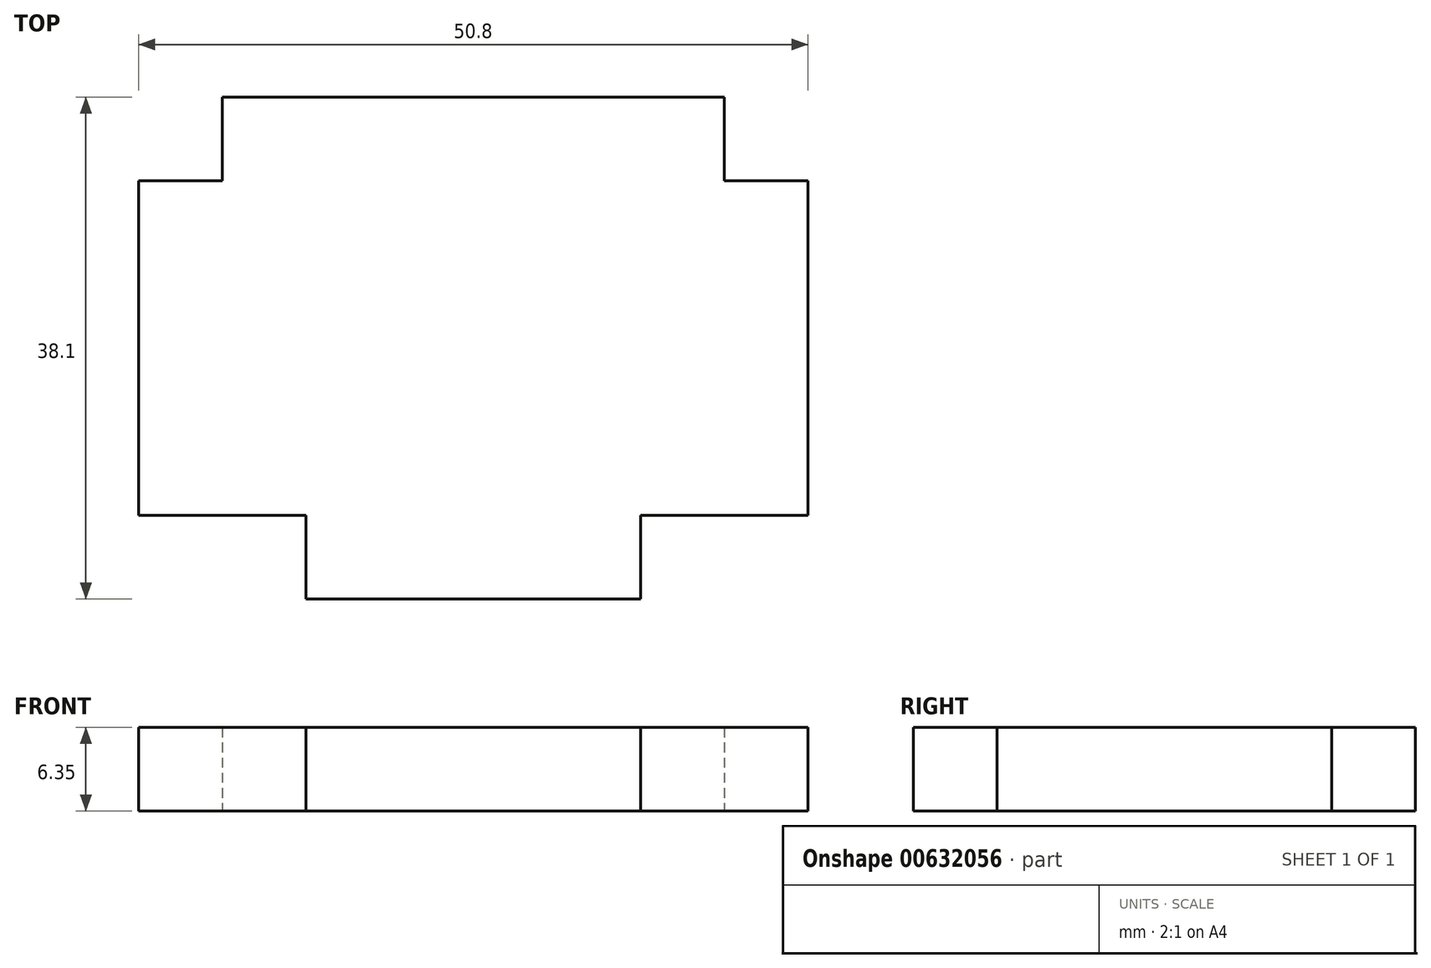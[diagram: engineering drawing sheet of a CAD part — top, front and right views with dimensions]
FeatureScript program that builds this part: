
annotation { "Feature Type Name" : "Feature", "Feature Type Description" : "" }
export const myFeature = defineFeature(function(context is Context, id is Id, definition is map)
    precondition{}
    {
        {
            var Q0;
            Q0=qCreatedBy(makeId("Top.planeOp"),FACE);
            var sketch = newSketch(context, id + "F0", { "sketchPlane" : qUnion([Q0])});
            skLineSegment(sketch, "E0.bottom", {"start": v(24.76, -5.52) * mm, "end": v(62.86, -5.52) * mm});
            skLineSegment(sketch, "E0.top", {"start": v(24.76, -43.62) * mm, "end": v(62.86, -43.62) * mm});
            skLineSegment(sketch, "E0.left", {"start": v(24.76, -5.52) * mm, "end": v(24.76, -43.62) * mm});
            skLineSegment(sketch, "E0.right", {"start": v(62.86, -5.52) * mm, "end": v(62.86, -43.62) * mm});
            skSolve(sketch);
        }
        {
            var Q0;
            Q0=makeQuery(id+"F0.imprint","IMPRINT",FACE,{"disambiguationData":[TD([[makeQuery(id+"F0.imprint","IMPRINT",EDGE,{"derivedFrom":sQuery(id+"F0.wireOp",EDGE,"E0.bottom")}),-1.0]])]});
            extrude(context, id + "F1", {"entities" : qUnion([Q0]), "depth" : 6.35 * mm, "offsetDistance" : 25.4 * mm});
        }
        {
            var Q0;
            Q0=makeQuery(id+"F1.opExtrude","SWEPT_FACE",FACE,{"disambiguationData":[OSD([sQuery(id+"F0.wireOp",EDGE,"E0.right")])]});
            var sketch = newSketch(context, id + "F2", { "sketchPlane" : qUnion([Q0])});
            skLineSegment(sketch, "E1.bottom", {"start": v(-5.52, 6.35) * mm, "end": v(-11.87, 6.35) * mm});
            skLineSegment(sketch, "E1.top", {"start": v(-5.52, 0) * mm, "end": v(-11.87, 0) * mm});
            skLineSegment(sketch, "E1.left", {"start": v(-5.52, 6.35) * mm, "end": v(-5.52, 0) * mm});
            skLineSegment(sketch, "E1.right", {"start": v(-11.87, 6.35) * mm, "end": v(-11.87, 0) * mm});
            skLineSegment(sketch, "E2.bottom", {"start": v(-43.62, 0) * mm, "end": v(-37.27, 0) * mm});
            skLineSegment(sketch, "E2.top", {"start": v(-43.62, 6.35) * mm, "end": v(-37.27, 6.35) * mm});
            skLineSegment(sketch, "E2.left", {"start": v(-43.62, 0) * mm, "end": v(-43.62, 6.35) * mm});
            skLineSegment(sketch, "E2.right", {"start": v(-37.27, 0) * mm, "end": v(-37.27, 6.35) * mm});
            skSolve(sketch);
        }
        {
            var Q0;
            Q0=makeQuery(id+"F1.opExtrude","SWEPT_FACE",FACE,{"disambiguationData":[OSD([sQuery(id+"F0.wireOp",EDGE,"E0.left")])]});
            var sketch = newSketch(context, id + "F3", { "sketchPlane" : qUnion([Q0])});
            skLineSegment(sketch, "E3.bottom", {"start": v(43.62, 0) * mm, "end": v(37.27, 0) * mm});
            skLineSegment(sketch, "E3.top", {"start": v(43.62, 6.35) * mm, "end": v(37.27, 6.35) * mm});
            skLineSegment(sketch, "E3.left", {"start": v(43.62, 0) * mm, "end": v(43.62, 6.35) * mm});
            skLineSegment(sketch, "E3.right", {"start": v(37.27, 0) * mm, "end": v(37.27, 6.35) * mm});
            skLineSegment(sketch, "E4.bottom", {"start": v(5.52, 0) * mm, "end": v(11.87, 0) * mm});
            skLineSegment(sketch, "E4.top", {"start": v(5.52, 6.35) * mm, "end": v(11.87, 6.35) * mm});
            skLineSegment(sketch, "E4.left", {"start": v(5.52, 0) * mm, "end": v(5.52, 6.35) * mm});
            skLineSegment(sketch, "E4.right", {"start": v(11.87, 0) * mm, "end": v(11.87, 6.35) * mm});
            skSolve(sketch);
        }
        {
            var Q0;
            {var subQ0=sQuery(id+"F2.wireOp",EDGE,"E1.right");Q0=makeQuery(id+"F2.imprint","IMPRINT",FACE,{"disambiguationData":[TD([[makeQuery(id+"F2.imprint","IMPRINT",EDGE,{"derivedFrom":subQ0}),-1.0]])]});}
            extrude(context, id + "F4", {"entities" : qUnion([Q0]), "operationType" : NewBodyOperationType.ADD, "depth" : 6.35 * mm, "offsetDistance" : 25.4 * mm});
        }
        {
            var Q0;
            {var subQ0=sQuery(id+"F3.wireOp",EDGE,"E3.right");Q0=makeQuery(id+"F3.imprint","IMPRINT",FACE,{"disambiguationData":[TD([[makeQuery(id+"F3.imprint","IMPRINT",EDGE,{"derivedFrom":subQ0}),1.0]])]});}
            extrude(context, id + "F5", {"entities" : qUnion([Q0]), "operationType" : NewBodyOperationType.ADD, "depth" : 6.35 * mm, "offsetDistance" : 25.4 * mm});
        }
        {
            var Q0;
            {var subQ0=sQuery(id+"F0.wireOp",EDGE,"E0.top");var subQ2=sQuery(id+"F0.wireOp",EDGE,"E0.right");Q0=makeQuery(id+"F4.boolean.opBoolean","SPLIT",FACE,{"disambiguationData":[TD([makeQuery(id+"F1.opExtrude","SWEPT_FACE",FACE,{"disambiguationData":[OSD([subQ0])]})])],"derivedFrom":makeQuery(id+"F1.opExtrude","SWEPT_FACE",FACE,{"disambiguationData":[OSD([subQ2])]})});}
            extrude(context, id + "F6", {"entities" : qUnion([Q0]), "operationType" : NewBodyOperationType.REMOVE, "oppositeDirection" : true, "depth" : 6.35 * mm, "offsetDistance" : 25.4 * mm});
        }
        {
            var Q0;
            {var subQ4=sQuery(id+"F0.wireOp",EDGE,"E0.left");var subQ5=sQuery(id+"F0.wireOp",EDGE,"E0.top");Q0=makeQuery(id+"F5.boolean.opBoolean","SPLIT",FACE,{"disambiguationData":[TD([makeQuery(id+"F1.opExtrude","SWEPT_FACE",FACE,{"disambiguationData":[OSD([subQ5])]})])],"derivedFrom":makeQuery(id+"F1.opExtrude","SWEPT_FACE",FACE,{"disambiguationData":[OSD([subQ4])]})});}
            extrude(context, id + "F7", {"entities" : qUnion([Q0]), "operationType" : NewBodyOperationType.REMOVE, "oppositeDirection" : true, "depth" : 6.35 * mm, "offsetDistance" : 25.4 * mm});
        }
    });
